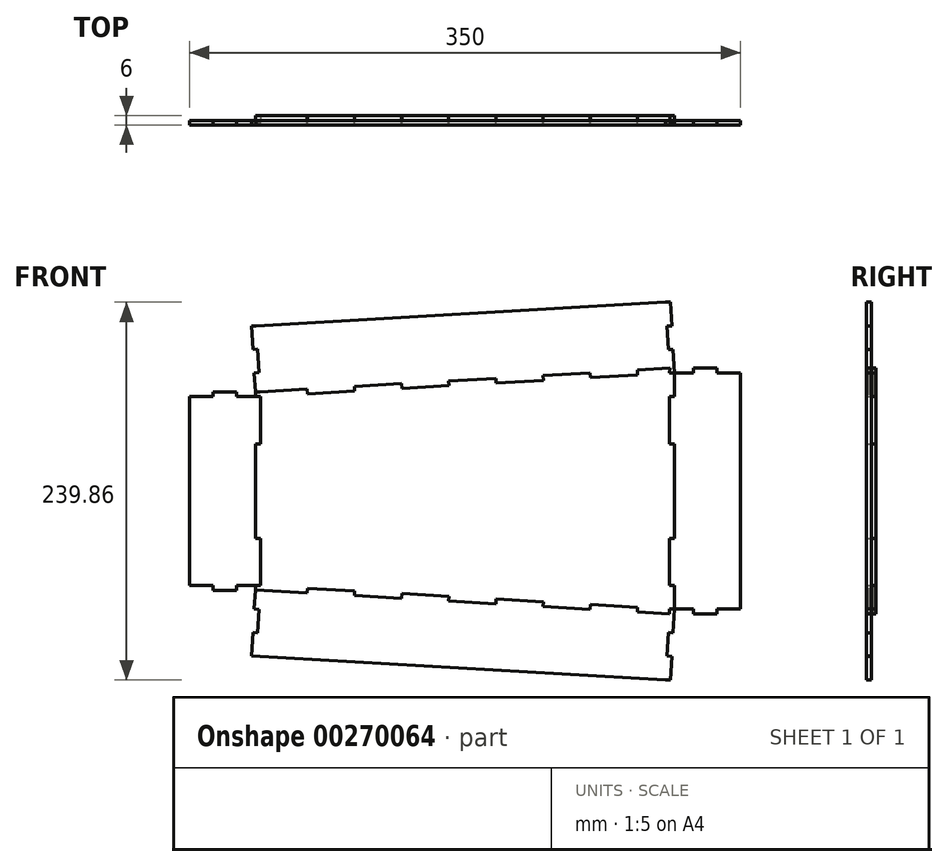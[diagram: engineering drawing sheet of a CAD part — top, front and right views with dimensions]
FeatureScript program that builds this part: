
annotation { "Feature Type Name" : "Feature", "Feature Type Description" : "" }
export const myFeature = defineFeature(function(context is Context, id is Id, definition is map)
    precondition{}
    {
        {
            var Q0;
            Q0=qCreatedBy(makeId("Front.planeOp"),FACE);
            var sketch = newSketch(context, id + "F0", { "sketchPlane" : qUnion([Q0])});
            skLineSegment(sketch, "E0", {"start": v(0, 0) * mm, "end": v(-130, 0) * mm, "construction": true});
            skLineSegment(sketch, "E1", {"start": v(0, 0) * mm, "end": v(130, 0) * mm, "construction": true});
            skLineSegment(sketch, "E2", {"start": v(130, 0) * mm, "end": v(130, 75) * mm, "construction": true});
            skLineSegment(sketch, "E3", {"start": v(-130, 0) * mm, "end": v(-130, 60) * mm, "construction": true});
            skLineSegment(sketch, "E4", {"start": v(-130, 60) * mm, "end": v(130, 75) * mm, "construction": true});
            skLineSegment(sketch, "E5.0", {"start": v(-133, 0) * mm, "end": v(-133, 60) * mm, "construction": true});
            skLineSegment(sketch, "E6.0", {"start": v(133, 0) * mm, "end": v(133, 75) * mm, "construction": true});
            skLineSegment(sketch, "E7", {"start": v(-100.22, 64.73) * mm, "end": v(-130.17, 63) * mm});
            skLineSegment(sketch, "E8", {"start": v(-100.22, 64.73) * mm, "end": v(-100.05, 61.73) * mm});
            skLineSegment(sketch, "E9", {"start": v(-100.05, 61.73) * mm, "end": v(-70.1, 63.46) * mm});
            skLineSegment(sketch, "E10", {"start": v(-70.1, 63.46) * mm, "end": v(-70.27, 66.45) * mm});
            skLineSegment(sketch, "E11", {"start": v(-70.27, 66.45) * mm, "end": v(-40.32, 68.18) * mm});
            skLineSegment(sketch, "E12", {"start": v(-40.32, 68.18) * mm, "end": v(-40.15, 65.18) * mm});
            skLineSegment(sketch, "E13", {"start": v(-40.15, 65.18) * mm, "end": v(-10.2, 66.91) * mm});
            skLineSegment(sketch, "E14", {"start": v(-10.2, 66.91) * mm, "end": v(-10.37, 69.9) * mm});
            skLineSegment(sketch, "E15", {"start": v(-10.37, 69.9) * mm, "end": v(19.58, 71.63) * mm});
            skLineSegment(sketch, "E16", {"start": v(19.58, 71.63) * mm, "end": v(19.75, 68.64) * mm});
            skLineSegment(sketch, "E17", {"start": v(19.75, 68.64) * mm, "end": v(49.7, 70.37) * mm});
            skLineSegment(sketch, "E18", {"start": v(49.7, 70.37) * mm, "end": v(49.53, 73.36) * mm});
            skLineSegment(sketch, "E19", {"start": v(49.53, 73.36) * mm, "end": v(79.48, 75.1) * mm});
            skLineSegment(sketch, "E20", {"start": v(79.48, 75.1) * mm, "end": v(79.65, 72.1) * mm});
            skLineSegment(sketch, "E21", {"start": v(79.65, 72.1) * mm, "end": v(109.6, 73.82) * mm});
            skLineSegment(sketch, "E22", {"start": v(130, 75) * mm, "end": v(129.92, 76.4) * mm});
            skLineSegment(sketch, "E23.0", {"start": v(-132.6, 104.93) * mm, "end": v(127.4, 119.93) * mm});
            skLineSegment(sketch, "E24", {"start": v(129.15, 89.8) * mm, "end": v(128.28, 104.78) * mm});
            skLineSegment(sketch, "E25", {"start": v(-131.74, 90.13) * mm, "end": v(-130.88, 75.15) * mm});
            skLineSegment(sketch, "E26", {"start": v(-130, 0) * mm, "end": v(-133, 0) * mm});
            skLineSegment(sketch, "E27", {"start": v(-133, 0) * mm, "end": v(-133, 30) * mm});
            skLineSegment(sketch, "E28", {"start": v(-133, 30) * mm, "end": v(-130, 30) * mm});
            skLineSegment(sketch, "E29", {"start": v(-130, 30) * mm, "end": v(-130, 60) * mm});
            skLineSegment(sketch, "E30", {"start": v(130, 0) * mm, "end": v(133, 0) * mm});
            skLineSegment(sketch, "E31", {"start": v(133, 0) * mm, "end": v(133, 30) * mm});
            skLineSegment(sketch, "E32", {"start": v(133, 30) * mm, "end": v(130, 30) * mm});
            skLineSegment(sketch, "E33", {"start": v(130, 30) * mm, "end": v(130, 60) * mm});
            skLineSegment(sketch, "E34", {"start": v(130, 60) * mm, "end": v(133, 60) * mm});
            skLineSegment(sketch, "E35", {"start": v(133, 60) * mm, "end": v(133, 75) * mm});
            skLineSegment(sketch, "E36", {"start": v(130, 75) * mm, "end": v(133, 75) * mm});
            skLineSegment(sketch, "E37.0", {"start": v(175, 0) * mm, "end": v(175, 75) * mm});
            skLineSegment(sketch, "E38.0", {"start": v(-175, 0) * mm, "end": v(-175, 60) * mm});
            skLineSegment(sketch, "E39", {"start": v(-175, 60) * mm, "end": v(-160.17, 60) * mm});
            skLineSegment(sketch, "E40", {"start": v(-130, 60) * mm, "end": v(-145, 60) * mm});
            skLineSegment(sketch, "E41", {"start": v(-145, 60) * mm, "end": v(-145.17, 63) * mm});
            skLineSegment(sketch, "E42", {"start": v(-145.17, 63) * mm, "end": v(-160.17, 63) * mm});
            skLineSegment(sketch, "E43", {"start": v(-160.17, 63) * mm, "end": v(-160.17, 60) * mm});
            skLineSegment(sketch, "E44.trimOffspring", {"start": v(-145, 60) * mm, "end": v(-130, 60) * mm});
            skLineSegment(sketch, "E45.0", {"start": v(-135.6, 104.93) * mm, "end": v(-134.73, 89.95) * mm});
            skLineSegment(sketch, "E46", {"start": v(-133.34, 65.75) * mm, "end": v(-133, 60) * mm});
            skLineSegment(sketch, "E47", {"start": v(-133, 60) * mm, "end": v(-133.87, 74.97) * mm});
            skLineSegment(sketch, "E48", {"start": v(-133.87, 74.97) * mm, "end": v(-130.88, 75.15) * mm});
            skLineSegment(sketch, "E49", {"start": v(-130.88, 75.15) * mm, "end": v(-131.74, 90.13) * mm});
            skLineSegment(sketch, "E50", {"start": v(-131.74, 90.13) * mm, "end": v(-134.73, 89.95) * mm});
            skLineSegment(sketch, "E51", {"start": v(-134.73, 89.95) * mm, "end": v(-135.6, 104.93) * mm});
            skLineSegment(sketch, "E52", {"start": v(-135.6, 104.93) * mm, "end": v(-132.6, 104.93) * mm});
            skLineSegment(sketch, "E53.trimOffspring", {"start": v(-133.87, 74.97) * mm, "end": v(-133.34, 65.75) * mm});
            skLineSegment(sketch, "E54.0", {"start": v(132.91, 76.58) * mm, "end": v(132.14, 89.98) * mm});
            skLineSegment(sketch, "E55", {"start": v(133, 75) * mm, "end": v(132.91, 76.58) * mm});
            skLineSegment(sketch, "E56", {"start": v(133, 75) * mm, "end": v(132.14, 89.98) * mm});
            skLineSegment(sketch, "E57", {"start": v(132.14, 89.98) * mm, "end": v(129.15, 89.8) * mm});
            skLineSegment(sketch, "E58", {"start": v(128.28, 104.78) * mm, "end": v(131.28, 104.95) * mm});
            skLineSegment(sketch, "E59", {"start": v(131.28, 104.95) * mm, "end": v(130.41, 119.93) * mm});
            skLineSegment(sketch, "E60", {"start": v(130.41, 119.93) * mm, "end": v(127.4, 119.93) * mm});
            skLineSegment(sketch, "E61.trimOffspring", {"start": v(131.28, 104.95) * mm, "end": v(130.5, 118.51) * mm});
            skLineSegment(sketch, "E62", {"start": v(133, 75) * mm, "end": v(145, 75) * mm});
            skLineSegment(sketch, "E63", {"start": v(130, 75) * mm, "end": v(145, 75) * mm});
            skLineSegment(sketch, "E64", {"start": v(145, 75) * mm, "end": v(145, 78) * mm});
            skLineSegment(sketch, "E65", {"start": v(145, 78) * mm, "end": v(160, 78) * mm});
            skLineSegment(sketch, "E66", {"start": v(160, 78) * mm, "end": v(160, 75) * mm});
            skLineSegment(sketch, "E67", {"start": v(160, 75) * mm, "end": v(175, 75) * mm});
            skLineSegment(sketch, "E68", {"start": v(-175, 0) * mm, "end": v(175, 0) * mm, "construction": true});
            skLineSegment(sketch, "E69.MirrorCS", {"start": v(133, -75) * mm, "end": v(132.91, -76.58) * mm});
            skLineSegment(sketch, "E70.MirrorCS", {"start": v(130, -75) * mm, "end": v(129.92, -76.4) * mm});
            skLineSegment(sketch, "E71.MirrorCS", {"start": v(130, -75) * mm, "end": v(133, -75) * mm});
            skLineSegment(sketch, "E72.MirrorCS", {"start": v(-133.34, -65.75) * mm, "end": v(-133, -60) * mm});
            skLineSegment(sketch, "E73.MirrorCS", {"start": v(-133.87, -74.97) * mm, "end": v(-130.88, -75.15) * mm});
            skLineSegment(sketch, "E74.MirrorCS", {"start": v(-135.6, -104.93) * mm, "end": v(-134.73, -89.95) * mm});
            skLineSegment(sketch, "E75.MirrorCS", {"start": v(-130, -60) * mm, "end": v(-145, -60) * mm});
            skLineSegment(sketch, "E76.MirrorCS", {"start": v(-133.87, -74.97) * mm, "end": v(-133.34, -65.75) * mm});
            skLineSegment(sketch, "E77.MirrorCS", {"start": v(129.15, -89.8) * mm, "end": v(128.28, -104.78) * mm});
            skLineSegment(sketch, "E78.MirrorCS", {"start": v(-133, -60) * mm, "end": v(-133.87, -74.97) * mm});
            skLineSegment(sketch, "E79.MirrorCS", {"start": v(-145, -60) * mm, "end": v(-130, -60) * mm});
            skLineSegment(sketch, "E80.MirrorCS", {"start": v(-134.73, -89.95) * mm, "end": v(-135.6, -104.93) * mm});
            skLineSegment(sketch, "E81.MirrorCS", {"start": v(-130.88, -75.15) * mm, "end": v(-131.74, -90.13) * mm});
            skLineSegment(sketch, "E82.MirrorCS", {"start": v(132.14, -89.98) * mm, "end": v(129.15, -89.8) * mm});
            skLineSegment(sketch, "E83.MirrorCS", {"start": v(-145, -60) * mm, "end": v(-145.17, -63) * mm});
            skLineSegment(sketch, "E84.MirrorCS", {"start": v(-131.74, -90.13) * mm, "end": v(-134.73, -89.95) * mm});
            skLineSegment(sketch, "E85.MirrorCS", {"start": v(133, -75) * mm, "end": v(132.14, -89.98) * mm});
            skLineSegment(sketch, "E86.MirrorCS", {"start": v(133, -75) * mm, "end": v(145, -75) * mm});
            skLineSegment(sketch, "E87.MirrorCS", {"start": v(160, -75) * mm, "end": v(175, -75) * mm});
            skLineSegment(sketch, "E88.MirrorCS", {"start": v(128.28, -104.78) * mm, "end": v(131.28, -104.95) * mm});
            skLineSegment(sketch, "E89.MirrorCS", {"start": v(131.28, -104.95) * mm, "end": v(130.41, -119.93) * mm});
            skLineSegment(sketch, "E90.MirrorCS", {"start": v(132.91, -76.58) * mm, "end": v(132.14, -89.98) * mm});
            skLineSegment(sketch, "E91.MirrorCS", {"start": v(130.41, -119.93) * mm, "end": v(127.4, -119.93) * mm});
            skLineSegment(sketch, "E92.MirrorCS", {"start": v(131.28, -104.95) * mm, "end": v(130.5, -118.51) * mm});
            skLineSegment(sketch, "E93.MirrorCS", {"start": v(160, -78) * mm, "end": v(160, -75) * mm});
            skLineSegment(sketch, "E94.MirrorCS", {"start": v(130, -75) * mm, "end": v(145, -75) * mm});
            skLineSegment(sketch, "E95.MirrorCS", {"start": v(-131.74, -90.13) * mm, "end": v(-130.88, -75.15) * mm});
            skLineSegment(sketch, "E96.MirrorCS", {"start": v(-160.17, -63) * mm, "end": v(-160.17, -60) * mm});
            skLineSegment(sketch, "E97.MirrorCS", {"start": v(145, -75) * mm, "end": v(145, -78) * mm});
            skLineSegment(sketch, "E98.MirrorCS", {"start": v(-175, -60) * mm, "end": v(-160.17, -60) * mm});
            skLineSegment(sketch, "E99.MirrorCS", {"start": v(49.7, -70.37) * mm, "end": v(49.53, -73.36) * mm});
            skLineSegment(sketch, "E100.MirrorCS", {"start": v(133, -30) * mm, "end": v(130, -30) * mm});
            skLineSegment(sketch, "E101.MirrorCS", {"start": v(-40.32, -68.18) * mm, "end": v(-40.15, -65.18) * mm});
            skLineSegment(sketch, "E102.MirrorCS", {"start": v(-133, -30) * mm, "end": v(-130, -30) * mm});
            skLineSegment(sketch, "E103.MirrorCS", {"start": v(133, -60) * mm, "end": v(133, -75) * mm});
            skLineSegment(sketch, "E104.MirrorCS", {"start": v(145, -78) * mm, "end": v(160, -78) * mm});
            skLineSegment(sketch, "E105.MirrorCS", {"start": v(-10.2, -66.91) * mm, "end": v(-10.37, -69.9) * mm});
            skLineSegment(sketch, "E106.MirrorCS", {"start": v(-145.17, -63) * mm, "end": v(-160.17, -63) * mm});
            skLineSegment(sketch, "E107.MirrorCS", {"start": v(130, -60) * mm, "end": v(133, -60) * mm});
            skLineSegment(sketch, "E108.MirrorCS", {"start": v(19.58, -71.63) * mm, "end": v(19.75, -68.64) * mm});
            skLineSegment(sketch, "E109.MirrorCS", {"start": v(79.48, -75.1) * mm, "end": v(79.65, -72.1) * mm});
            skLineSegment(sketch, "E110.MirrorCS", {"start": v(-70.1, -63.46) * mm, "end": v(-70.27, -66.45) * mm});
            skLineSegment(sketch, "E111.MirrorCS", {"start": v(-100.22, -64.73) * mm, "end": v(-100.05, -61.73) * mm});
            skLineSegment(sketch, "E112.MirrorCS", {"start": v(133, 0) * mm, "end": v(133, -30) * mm});
            skLineSegment(sketch, "E113.MirrorCS", {"start": v(19.75, -68.64) * mm, "end": v(49.7, -70.37) * mm});
            skLineSegment(sketch, "E114.MirrorCS", {"start": v(79.65, -72.1) * mm, "end": v(109.6, -73.82) * mm});
            skLineSegment(sketch, "E115.MirrorCS", {"start": v(-40.15, -65.18) * mm, "end": v(-10.2, -66.91) * mm});
            skLineSegment(sketch, "E116.MirrorCS", {"start": v(130, 0) * mm, "end": v(130, -75) * mm, "construction": true});
            skLineSegment(sketch, "E117.MirrorCS", {"start": v(130, -30) * mm, "end": v(130, -60) * mm});
            skLineSegment(sketch, "E118.MirrorCS", {"start": v(-10.37, -69.9) * mm, "end": v(19.58, -71.63) * mm});
            skLineSegment(sketch, "E119.MirrorCS", {"start": v(49.53, -73.36) * mm, "end": v(79.48, -75.1) * mm});
            skLineSegment(sketch, "E120.MirrorCS", {"start": v(-70.27, -66.45) * mm, "end": v(-40.32, -68.18) * mm});
            skLineSegment(sketch, "E121.MirrorCS", {"start": v(-100.22, -64.73) * mm, "end": v(-133.17, -62.83) * mm});
            skLineSegment(sketch, "E122.MirrorCS", {"start": v(-133, 0) * mm, "end": v(-133, -30) * mm});
            skLineSegment(sketch, "E123.MirrorCS", {"start": v(-100.05, -61.73) * mm, "end": v(-70.1, -63.46) * mm});
            skLineSegment(sketch, "E124.MirrorCS", {"start": v(-135.59, -104.75) * mm, "end": v(127.4, -119.93) * mm});
            skLineSegment(sketch, "E125.MirrorCS", {"start": v(-175, 0) * mm, "end": v(-175, -60) * mm});
            skLineSegment(sketch, "E126.MirrorCS", {"start": v(-130, -30) * mm, "end": v(-130, -60) * mm});
            skLineSegment(sketch, "E127.MirrorCS", {"start": v(-130, -60) * mm, "end": v(130, -75) * mm, "construction": true});
            skLineSegment(sketch, "E128.MirrorCS", {"start": v(-133, 0) * mm, "end": v(-133, -60) * mm, "construction": true});
            skLineSegment(sketch, "E129.MirrorCS", {"start": v(-130, 0) * mm, "end": v(-130, -60) * mm, "construction": true});
            skLineSegment(sketch, "E130.MirrorCS", {"start": v(133, 0) * mm, "end": v(133, -75) * mm, "construction": true});
            skLineSegment(sketch, "E131.MirrorCS", {"start": v(175, 0) * mm, "end": v(175, -75) * mm});
            skPoint(sketch, "E132.orphan", {"position": v(-132.6, -104.93) * mm});
            skLineSegment(sketch, "E133", {"start": v(109.6, 73.82) * mm, "end": v(109.43, 76.82) * mm});
            skLineSegment(sketch, "E134", {"start": v(109.43, 76.82) * mm, "end": v(130.02, 78) * mm});
            skLineSegment(sketch, "E135", {"start": v(130.02, 78) * mm, "end": v(130, 75) * mm});
            skLineSegment(sketch, "E136", {"start": v(109.6, -73.82) * mm, "end": v(109.43, -76.82) * mm});
            skLineSegment(sketch, "E137", {"start": v(109.43, -76.82) * mm, "end": v(129.92, -78) * mm});
            skLineSegment(sketch, "E138", {"start": v(129.92, -78) * mm, "end": v(130, -75) * mm});
            skLineSegment(sketch, "E139", {"start": v(-130.17, 63) * mm, "end": v(-133.16, 62.83) * mm});
            skSolve(sketch);
        }
        {
            var Q0;
            Q0=makeQuery(id+"F0.imprint","IMPRINT",FACE,{"disambiguationData":[TD([[makeQuery(id+"F0.imprint","IMPRINT",EDGE,{"derivedFrom":sQuery(id+"F0.wireOp",EDGE,"E27")}),1.0]])]});
            var Q1;
            {var subQ4=sQuery(id+"F0.wireOp",EDGE,"E73.MirrorCS");Q1=makeQuery(id+"F0.imprint","IMPRINT",FACE,{"disambiguationData":[TD([[makeQuery(id+"F0.imprint","IMPRINT",EDGE,{"derivedFrom":subQ4}),1.0]])]});}
            var Q2;
            Q2=makeQuery(id+"F0.imprint","IMPRINT",FACE,{"disambiguationData":[TD([[makeQuery(id+"F0.imprint","IMPRINT",EDGE,{"derivedFrom":sQuery(id+"F0.wireOp",EDGE,"E7")}),-1.0]])]});
            var Q3;
            Q3=makeQuery(id+"F0.imprint","IMPRINT",FACE,{"disambiguationData":[TD([[makeQuery(id+"F0.imprint","IMPRINT",EDGE,{"derivedFrom":sQuery(id+"F0.wireOp",EDGE,"E31")}),-1.0]])]});
            extrude(context, id + "F1", {"entities" : qUnion([Q0, Q1, Q2, Q3]), "depth" : 3 * mm});
        }
        {
            var Q0;
            Q0=makeQuery(id+"F0.imprint","IMPRINT",FACE,{"disambiguationData":[TD([[makeQuery(id+"F0.imprint","IMPRINT",EDGE,{"derivedFrom":sQuery(id+"F0.wireOp",EDGE,"E7")}),1.0]])]});
            extrude(context, id + "F2", {"entities" : qUnion([Q0]), "oppositeDirection" : true, "depth" : 3 * mm});
        }
    });
